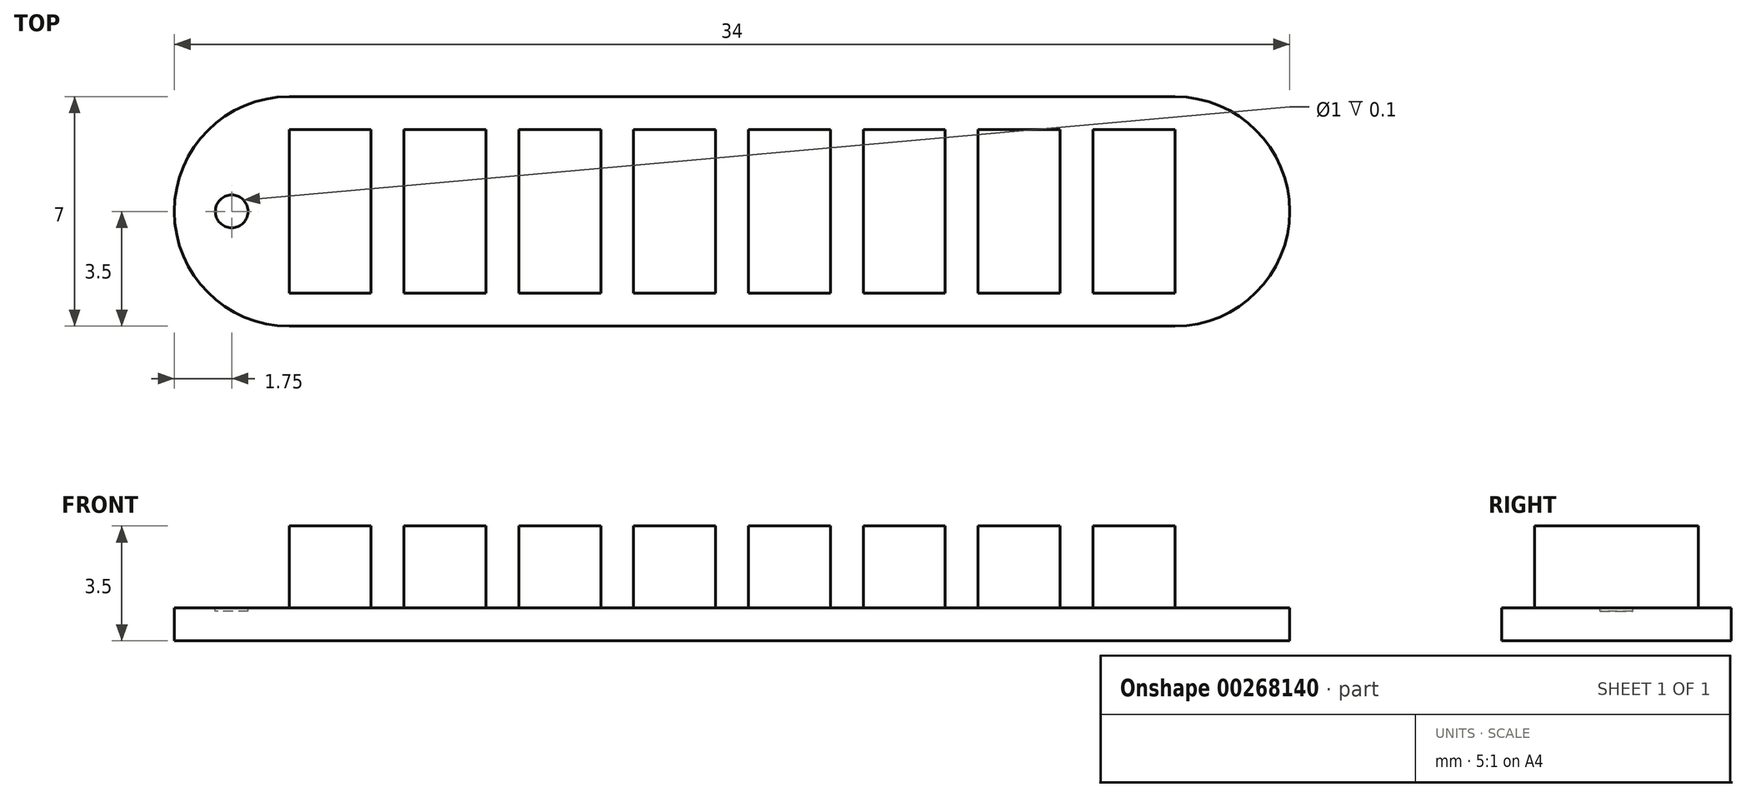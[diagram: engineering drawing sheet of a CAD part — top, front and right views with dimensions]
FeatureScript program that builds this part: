
annotation { "Feature Type Name" : "Feature", "Feature Type Description" : "" }
export const myFeature = defineFeature(function(context is Context, id is Id, definition is map)
    precondition{}
    {
        {
            var Q0;
            Q0=qCreatedBy(makeId("Top.planeOp"),FACE);
            var sketch = newSketch(context, id + "F0", { "sketchPlane" : qUnion([Q0])});
            skArc(sketch, "E0", {"start": v(-13.5, 3.5) * mm, "mid": v(-17, 0) * mm, "end": v(-13.5, -3.5) * mm});
            skArc(sketch, "E1", {"start": v(13.5, -3.5) * mm, "mid": v(17, 0) * mm, "end": v(13.5, 3.5) * mm});
            skLineSegment(sketch, "E2", {"start": v(0, 3.5) * mm, "end": v(13.5, 3.5) * mm});
            skLineSegment(sketch, "E3", {"start": v(0, 3.5) * mm, "end": v(-13.5, 3.5) * mm});
            skLineSegment(sketch, "E4", {"start": v(0, -3.5) * mm, "end": v(-13.5, -3.5) * mm});
            skLineSegment(sketch, "E5", {"start": v(0, -3.5) * mm, "end": v(13.5, -3.5) * mm});
            skSolve(sketch);
        }
        {
            var Q0;
            Q0=makeQuery(id+"F0.imprint","IMPRINT",FACE,{"disambiguationData":[TD([[makeQuery(id+"F0.imprint","IMPRINT",EDGE,{"derivedFrom":sQuery(id+"F0.wireOp",EDGE,"E0")}),1.0]])]});
            var Q1;
            Q1=makeQuery(id+"F0.imprint","IMPRINT",FACE,{"disambiguationData":[TD([[makeQuery(id+"F0.imprint","IMPRINT",EDGE,{"derivedFrom":sQuery(id+"F0.wireOp",EDGE,"lyFTZzlh-rBqs-ufN0-1DFe-RjFTf2CyIcG0")}),1.0]])]});
            extrude(context, id + "F1", {"entities" : qUnion([Q0, Q1]), "depth" : 1 * mm, "offsetDistance" : 25 * mm});
        }
        {
            var Q0;
            Q0=makeQuery(id+"F1.opExtrude","CAP_FACE",FACE,{"disambiguationData":[OSD([sQuery(id+"F0.wireOp",EDGE,"E0"),sQuery(id+"F0.wireOp",EDGE,"E1"),sQuery(id+"F0.wireOp",EDGE,"E2"),sQuery(id+"F0.wireOp",EDGE,"E3"),sQuery(id+"F0.wireOp",EDGE,"E4"),sQuery(id+"F0.wireOp",EDGE,"E5")])],"isStart":false});
            var sketch = newSketch(context, id + "F2", { "sketchPlane" : qUnion([Q0])});
            skLineSegment(sketch, "E6", {"start": v(-13.5, 2.5) * mm, "end": v(-13.5, -2.5) * mm});
            skLineSegment(sketch, "E7", {"start": v(13.5, 2.5) * mm, "end": v(13.5, -2.5) * mm});
            skLineSegment(sketch, "E8", {"start": v(-13.5, 2.5) * mm, "end": v(-11, 2.5) * mm});
            skLineSegment(sketch, "E9", {"start": v(-10, 2.5) * mm, "end": v(-7.5, 2.5) * mm});
            skLineSegment(sketch, "E10", {"start": v(-6.5, 2.5) * mm, "end": v(-4, 2.5) * mm});
            skLineSegment(sketch, "E11", {"start": v(-3, 2.5) * mm, "end": v(-0.5, 2.5) * mm});
            skLineSegment(sketch, "E12", {"start": v(0.5, 2.5) * mm, "end": v(3, 2.5) * mm});
            skLineSegment(sketch, "E13", {"start": v(4, 2.5) * mm, "end": v(6.5, 2.5) * mm});
            skLineSegment(sketch, "E14", {"start": v(7.5, 2.5) * mm, "end": v(10, 2.5) * mm});
            skLineSegment(sketch, "E15", {"start": v(11, 2.5) * mm, "end": v(13.5, 2.5) * mm});
            skLineSegment(sketch, "E16", {"start": v(-13.5, -2.5) * mm, "end": v(-11, -2.5) * mm});
            skLineSegment(sketch, "E17", {"start": v(-10, -2.5) * mm, "end": v(-7.5, -2.5) * mm});
            skLineSegment(sketch, "E18", {"start": v(-6.5, -2.5) * mm, "end": v(-4, -2.5) * mm});
            skLineSegment(sketch, "E19", {"start": v(-3, -2.5) * mm, "end": v(-0.5, -2.5) * mm});
            skLineSegment(sketch, "E20", {"start": v(0.5, -2.5) * mm, "end": v(3, -2.5) * mm});
            skLineSegment(sketch, "E21", {"start": v(4, -2.5) * mm, "end": v(6.5, -2.5) * mm});
            skLineSegment(sketch, "E22", {"start": v(7.5, -2.5) * mm, "end": v(10, -2.5) * mm});
            skLineSegment(sketch, "E23", {"start": v(11, -2.5) * mm, "end": v(13.5, -2.5) * mm});
            skLineSegment(sketch, "E24", {"start": v(-11, 2.5) * mm, "end": v(-11, -2.5) * mm});
            skLineSegment(sketch, "E25", {"start": v(-10, 2.5) * mm, "end": v(-10, -2.5) * mm});
            skLineSegment(sketch, "E26", {"start": v(-7.5, 2.5) * mm, "end": v(-7.5, -2.5) * mm});
            skLineSegment(sketch, "E27", {"start": v(-6.5, 2.5) * mm, "end": v(-6.5, -2.5) * mm});
            skLineSegment(sketch, "E28", {"start": v(-4, 2.5) * mm, "end": v(-4, -2.5) * mm});
            skLineSegment(sketch, "E29", {"start": v(-3, 2.5) * mm, "end": v(-3, -2.5) * mm});
            skLineSegment(sketch, "E30", {"start": v(-0.5, 2.5) * mm, "end": v(-0.5, -2.5) * mm});
            skLineSegment(sketch, "E31", {"start": v(0.5, 2.5) * mm, "end": v(0.5, -2.5) * mm});
            skLineSegment(sketch, "E32", {"start": v(3, 2.5) * mm, "end": v(3, -2.5) * mm});
            skLineSegment(sketch, "E33", {"start": v(4, 2.5) * mm, "end": v(4, -2.5) * mm});
            skLineSegment(sketch, "E34", {"start": v(6.5, 2.5) * mm, "end": v(6.5, -2.5) * mm});
            skLineSegment(sketch, "E35", {"start": v(7.5, 2.5) * mm, "end": v(7.5, -2.5) * mm});
            skLineSegment(sketch, "E36", {"start": v(10, 2.5) * mm, "end": v(10, -2.5) * mm});
            skLineSegment(sketch, "E37", {"start": v(11, 2.5) * mm, "end": v(11, -2.5) * mm});
            skSolve(sketch);
        }
        {
            var Q0;
            Q0 = qSketchRegion(id + "F2", true);
            extrude(context, id + "F3", {"entities" : qUnion([Q0]), "operationType" : NewBodyOperationType.ADD, "depth" : 2.5 * mm, "offsetDistance" : 25 * mm});
        }
        {
            var Q0;
            Q0=makeQuery(id+"F1.opExtrude","CAP_FACE",FACE,{"disambiguationData":[OSD([sQuery(id+"F0.wireOp",EDGE,"E0"),sQuery(id+"F0.wireOp",EDGE,"E1"),sQuery(id+"F0.wireOp",EDGE,"E2"),sQuery(id+"F0.wireOp",EDGE,"E3"),sQuery(id+"F0.wireOp",EDGE,"E4"),sQuery(id+"F0.wireOp",EDGE,"E5")])],"isStart":false});
            var sketch = newSketch(context, id + "F4", { "sketchPlane" : qUnion([Q0])});
            skLineSegment(sketch, "E38", {"start": v(-17, 0) * mm, "end": v(-15.25, 0) * mm});
            skCircle(sketch, "E39", {"center": v(-15.25, 0) * mm, "radius": 0.5 * mm});
            skSolve(sketch);
        }
        {
            var Q0;
            Q0 = qSketchRegion(id + "F4", true);
            extrude(context, id + "F5", {"entities" : qUnion([Q0]), "operationType" : NewBodyOperationType.REMOVE, "oppositeDirection" : true, "depth" : 0.1 * mm, "offsetDistance" : 25 * mm});
        }
    });
